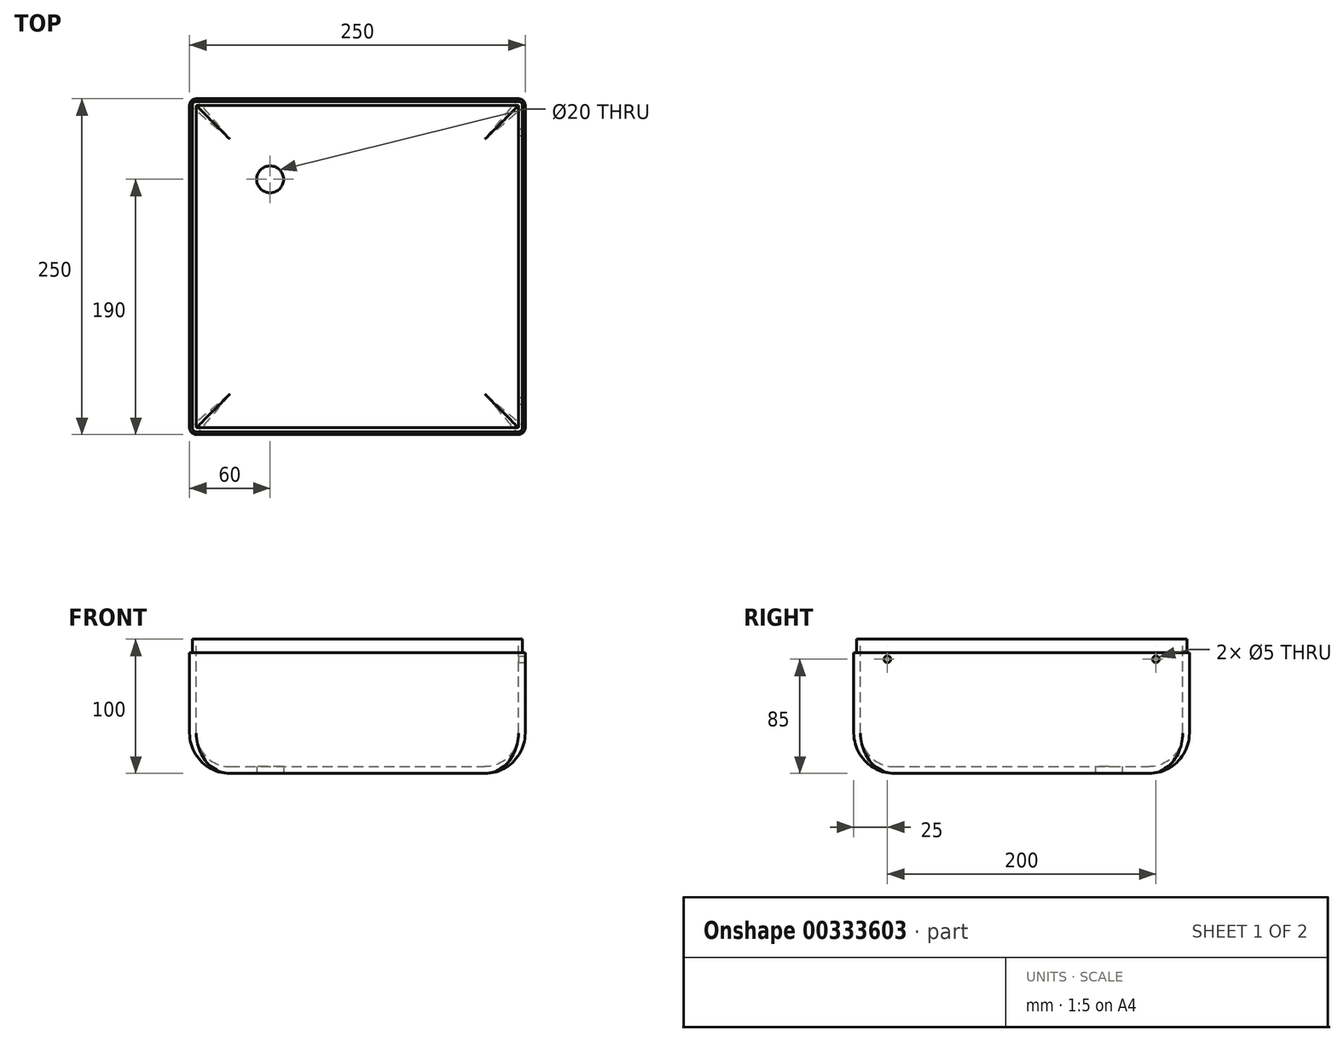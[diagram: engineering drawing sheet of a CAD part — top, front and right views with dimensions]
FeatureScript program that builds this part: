
annotation { "Feature Type Name" : "Feature", "Feature Type Description" : "" }
export const myFeature = defineFeature(function(context is Context, id is Id, definition is map)
    precondition{}
    {
        {
            var Q0;
            Q0=qCreatedBy(makeId("Top.planeOp"),FACE);
            var sketch = newSketch(context, id + "F0", { "sketchPlane" : qUnion([Q0])});
            skLineSegment(sketch, "E0.bottom", {"start": v(125, -125) * mm, "end": v(-125, -125) * mm});
            skLineSegment(sketch, "E0.top", {"start": v(125, 125) * mm, "end": v(-125, 125) * mm});
            skLineSegment(sketch, "E0.left", {"start": v(125, -125) * mm, "end": v(125, 125) * mm});
            skLineSegment(sketch, "E0.right", {"start": v(-125, -125) * mm, "end": v(-125, 125) * mm});
            skPoint(sketch, "E0.middle", {"position": v(0, 0) * mm});
            skSolve(sketch);
        }
        {
            var Q0;
            Q0=makeQuery(id+"F0.imprint","IMPRINT",FACE,{"disambiguationData":[TD([[makeQuery(id+"F0.imprint","IMPRINT",EDGE,{"derivedFrom":sQuery(id+"F0.wireOp",EDGE,"E0.bottom")}),-1.0]])]});
            extrude(context, id + "F1", {"entities" : qUnion([Q0]), "depth" : 100 * mm});
        }
        {
            var Q0;
            Q0=makeQuery(id+"F1.opExtrude","CAP_EDGE",EDGE,{"disambiguationData":[OSD([sQuery(id+"F0.wireOp",EDGE,"E0.bottom")])],"isStart":true});
            var Q1;
            Q1=makeQuery(id+"F1.opExtrude","CAP_EDGE",EDGE,{"disambiguationData":[OSD([sQuery(id+"F0.wireOp",EDGE,"E0.left")])],"isStart":true});
            var Q2;
            Q2=makeQuery(id+"F1.opExtrude","CAP_EDGE",EDGE,{"disambiguationData":[OSD([sQuery(id+"F0.wireOp",EDGE,"E0.top")])],"isStart":true});
            var Q3;
            Q3=makeQuery(id+"F1.opExtrude","CAP_EDGE",EDGE,{"disambiguationData":[OSD([sQuery(id+"F0.wireOp",EDGE,"E0.right")])],"isStart":true});
            fillet(context, id + "F2", {"entities" : qUnion([Q0, Q1, Q2, Q3]), "radius" : 30 * mm, "tangentPropagation" : true, "allowEdgeOverflow" : false});
        }
        {
            var Q0;
            Q0=makeQuery(id+"F1.opExtrude","SWEPT_EDGE",EDGE,{"disambiguationData":[OSD([sQuery(id+"F0.wireOp",EDGE,"E0.top"),sQuery(id+"F0.wireOp",EDGE,"E0.right")])]});
            var Q1;
            Q1=makeQuery(id+"F1.opExtrude","SWEPT_EDGE",EDGE,{"disambiguationData":[OSD([sQuery(id+"F0.wireOp",EDGE,"E0.top"),sQuery(id+"F0.wireOp",EDGE,"E0.left")])]});
            var Q2;
            Q2=makeQuery(id+"F1.opExtrude","SWEPT_EDGE",EDGE,{"disambiguationData":[OSD([sQuery(id+"F0.wireOp",EDGE,"E0.bottom"),sQuery(id+"F0.wireOp",EDGE,"E0.left")])]});
            var Q3;
            Q3=makeQuery(id+"F1.opExtrude","SWEPT_EDGE",EDGE,{"disambiguationData":[OSD([sQuery(id+"F0.wireOp",EDGE,"E0.bottom"),sQuery(id+"F0.wireOp",EDGE,"E0.right")])]});
            fillet(context, id + "F3", {"entities" : qUnion([Q0, Q1, Q2, Q3]), "radius" : 5 * mm, "tangentPropagation" : true, "allowEdgeOverflow" : false});
        }
        {
            var Q0;
            Q0=makeQuery(id+"F1.opExtrude","CAP_FACE",FACE,{"disambiguationData":[OSD([sQuery(id+"F0.wireOp",EDGE,"E0.bottom"),sQuery(id+"F0.wireOp",EDGE,"E0.top"),sQuery(id+"F0.wireOp",EDGE,"E0.left"),sQuery(id+"F0.wireOp",EDGE,"E0.right")])],"isStart":false});
            shell(context, id + "F4", {"entities" : qUnion([Q0]), "thickness" : 5 * mm});
        }
        {
            var Q0;
            Q0=makeQuery(id+"F1.opExtrude","CAP_FACE",FACE,{"disambiguationData":[OSD([sQuery(id+"F0.wireOp",EDGE,"E0.bottom"),sQuery(id+"F0.wireOp",EDGE,"E0.top"),sQuery(id+"F0.wireOp",EDGE,"E0.left"),sQuery(id+"F0.wireOp",EDGE,"E0.right")])],"isStart":false});
            var sketch = newSketch(context, id + "F5", { "sketchPlane" : qUnion([Q0])});
            skLineSegment(sketch, "E1.0", {"start": v(-125, -120) * mm, "end": v(-125, 120) * mm});
            skArc(sketch, "E1.1", {"start": v(-125, -120) * mm, "mid": v(-123.54, -123.54) * mm, "end": v(-120, -125) * mm});
            skLineSegment(sketch, "E1.2", {"start": v(120, -125) * mm, "end": v(-120, -125) * mm});
            skArc(sketch, "E1.3", {"start": v(120, -125) * mm, "mid": v(123.54, -123.54) * mm, "end": v(125, -120) * mm});
            skLineSegment(sketch, "E1.4", {"start": v(125, -120) * mm, "end": v(125, 120) * mm});
            skArc(sketch, "E1.5", {"start": v(125, 120) * mm, "mid": v(123.54, 123.54) * mm, "end": v(120, 125) * mm});
            skLineSegment(sketch, "E1.6", {"start": v(120, 125) * mm, "end": v(-120, 125) * mm});
            skArc(sketch, "E1.7", {"start": v(-120, 125) * mm, "mid": v(-123.54, 123.54) * mm, "end": v(-125, 120) * mm});
            skArc(sketch, "E2.0", {"start": v(123, 120) * mm, "mid": v(122.12, 122.12) * mm, "end": v(120, 123) * mm});
            skLineSegment(sketch, "E2.1", {"start": v(123, -120) * mm, "end": v(123, 120) * mm});
            skLineSegment(sketch, "E2.2", {"start": v(120, 123) * mm, "end": v(-120, 123) * mm});
            skArc(sketch, "E2.3", {"start": v(120, -123) * mm, "mid": v(122.12, -122.12) * mm, "end": v(123, -120) * mm});
            skArc(sketch, "E2.4", {"start": v(-120, 123) * mm, "mid": v(-122.12, 122.12) * mm, "end": v(-123, 120) * mm});
            skLineSegment(sketch, "E2.5", {"start": v(-123, -120) * mm, "end": v(-123, 120) * mm});
            skArc(sketch, "E2.6", {"start": v(-123, -120) * mm, "mid": v(-122.12, -122.12) * mm, "end": v(-120, -123) * mm});
            skLineSegment(sketch, "E2.7", {"start": v(120, -123) * mm, "end": v(-120, -123) * mm});
            skCircle(sketch, "E3", {"center": v(0, 0) * mm, "radius": 43.6 * mm});
            skSolve(sketch);
        }
        {
            var Q0;
            Q0=makeQuery(id+"F5.imprint","IMPRINT",FACE,{"disambiguationData":[TD([[makeQuery(id+"F5.imprint","IMPRINT",EDGE,{"derivedFrom":sQuery(id+"F5.wireOp",EDGE,"E1.0")}),-1.0]])]});
            extrude(context, id + "F6", {"entities" : qUnion([Q0]), "operationType" : NewBodyOperationType.REMOVE, "oppositeDirection" : true, "depth" : 10 * mm});
        }
        {
            var Q0;
            Q0=makeQuery(id+"F1.opExtrude","CAP_FACE",FACE,{"disambiguationData":[OSD([sQuery(id+"F0.wireOp",EDGE,"E0.bottom"),sQuery(id+"F0.wireOp",EDGE,"E0.top"),sQuery(id+"F0.wireOp",EDGE,"E0.left"),sQuery(id+"F0.wireOp",EDGE,"E0.right")])],"isStart":true});
            var sketch = newSketch(context, id + "F7", { "sketchPlane" : qUnion([Q0])});
            skCircle(sketch, "E4", {"center": v(0, 0) * mm, "radius": 46.97 * mm});
            skCircle(sketch, "E5", {"center": v(-65, -65) * mm, "radius": 10 * mm});
            skSolve(sketch);
        }
        {
            var Q0;
            Q0=makeQuery(id+"F1.opExtrude","SWEPT_FACE",FACE,{"disambiguationData":[OSD([sQuery(id+"F0.wireOp",EDGE,"E0.left")])]});
            var sketch = newSketch(context, id + "F8", { "sketchPlane" : qUnion([Q0])});
            skCircle(sketch, "E6", {"center": v(-100, 85) * mm, "radius": 2.5 * mm});
            skCircle(sketch, "E7", {"center": v(100, 85) * mm, "radius": 2.5 * mm});
            skSolve(sketch);
        }
        {
            var Q0;
            Q0=makeQuery(id+"F8.imprint","IMPRINT",FACE,{"disambiguationData":[TD([[makeQuery(id+"F8.imprint","IMPRINT",EDGE,{"derivedFrom":sQuery(id+"F8.wireOp",EDGE,"E6")}),1.0]])]});
            var Q1;
            Q1=makeQuery(id+"F8.imprint","IMPRINT",FACE,{"disambiguationData":[TD([[makeQuery(id+"F8.imprint","IMPRINT",EDGE,{"derivedFrom":sQuery(id+"F8.wireOp",EDGE,"E7")}),1.0]])]});
            extrude(context, id + "F9", {"entities" : qUnion([Q0, Q1]), "operationType" : NewBodyOperationType.REMOVE, "oppositeDirection" : true, "depth" : 6 * mm});
        }
        {
            var Q0;
            Q0=sQuery(id+"F7.wireOp",VERTEX,"E5.center");
            var Q1;
            Q1=makeQuery(id+"F1.opExtrude","SWEPT_BODY",BODY,{"disambiguationData":[OSD([sQuery(id+"F0.wireOp",EDGE,"E0.bottom"),sQuery(id+"F0.wireOp",EDGE,"E0.top"),sQuery(id+"F0.wireOp",EDGE,"E0.left"),sQuery(id+"F0.wireOp",EDGE,"E0.right")])]});
            hole(context, id + "F10", {"style" : HoleStyle.SIMPLE, "endStyle" : HoleEndStyle.THROUGH, "holeDiameter" : 20 * mm, "isTappedThrough" : true, "tappedDepth" : 12 * mm, "tapClearance" : 3, "locations" : qUnion([Q0]), "scope" : qUnion([Q1])});
        }
    });
